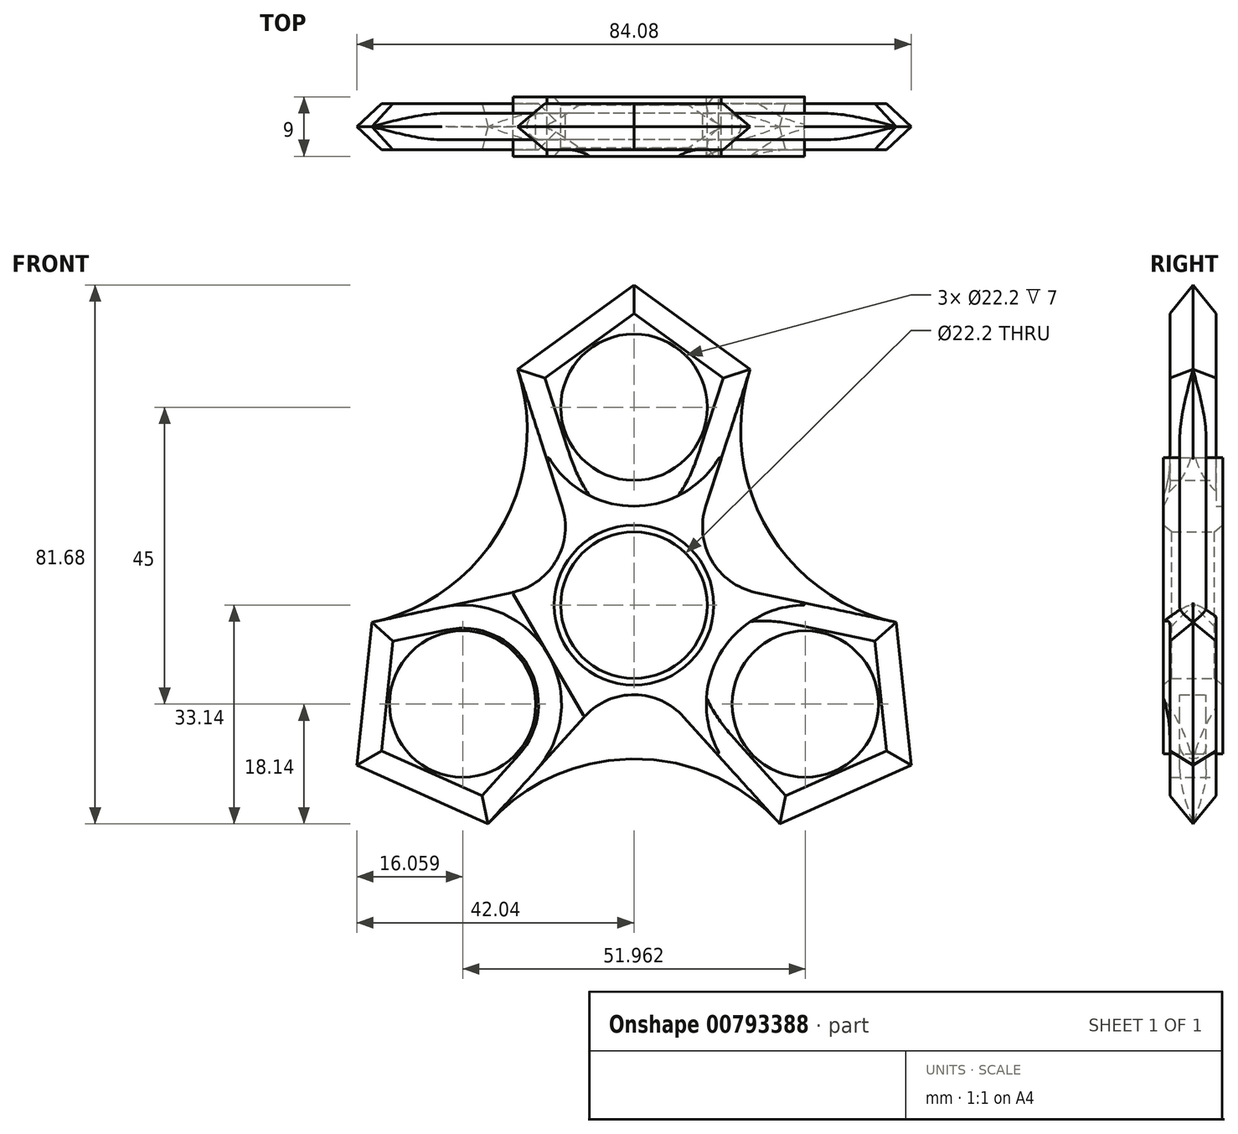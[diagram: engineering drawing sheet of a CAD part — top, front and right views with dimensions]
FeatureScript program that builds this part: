
annotation { "Feature Type Name" : "Feature", "Feature Type Description" : "" }
export const myFeature = defineFeature(function(context is Context, id is Id, definition is map)
    precondition{}
    {
        {
            var Q0;
            Q0=qCreatedBy(makeId("Front.planeOp"),FACE);
            var sketch = newSketch(context, id + "F0", { "sketchPlane" : qUnion([Q0])});
            skCircle(sketch, "E0", {"center": v(0, 0) * mm, "radius": 4 * mm});
            skCircle(sketch, "E1", {"center": v(0, 0) * mm, "radius": 11.1 * mm});
            skCircle(sketch, "E2", {"center": v(0, 30) * mm, "radius": 4 * mm});
            skCircle(sketch, "E3", {"center": v(0, 30) * mm, "radius": 11.1 * mm});
            skCircle(sketch, "E4.1.0", {"center": v(-25.98, -15) * mm, "radius": 11.1 * mm});
            skCircle(sketch, "E4.1.1", {"center": v(-25.98, -15) * mm, "radius": 4 * mm});
            skCircle(sketch, "E4.2.0", {"center": v(25.98, -15) * mm, "radius": 11.1 * mm});
            skCircle(sketch, "E4.2.1", {"center": v(25.98, -15) * mm, "radius": 4 * mm});
            skCircle(sketch, "E5.cCircle", {"center": v(0, 30) * mm, "radius": 15 * mm, "construction": true});
            skLineSegment(sketch, "E5.0", {"start": v(10.9, 15) * mm, "end": v(-10.9, 15) * mm});
            skLineSegment(sketch, "E5.1", {"start": v(-10.9, 15) * mm, "end": v(-17.63, 35.73) * mm});
            skLineSegment(sketch, "E5.2", {"start": v(-17.63, 35.73) * mm, "end": v(0, 48.54) * mm});
            skLineSegment(sketch, "E5.3", {"start": v(0, 48.54) * mm, "end": v(17.63, 35.73) * mm});
            skLineSegment(sketch, "E5.4", {"start": v(17.63, 35.73) * mm, "end": v(10.9, 15) * mm});
            skPoint(sketch, "E5.0.midPoint", {"position": v(0, 15) * mm});
            skLineSegment(sketch, "E6.1.0", {"start": v(-39.76, -2.6) * mm, "end": v(-18.44, 1.94) * mm});
            skLineSegment(sketch, "E6.1.2", {"start": v(-7.54, -16.94) * mm, "end": v(-22.13, -33.14) * mm});
            skLineSegment(sketch, "E6.1.3", {"start": v(-22.13, -33.14) * mm, "end": v(-42.04, -24.27) * mm});
            skLineSegment(sketch, "E6.1.4", {"start": v(-42.04, -24.27) * mm, "end": v(-39.76, -2.6) * mm});
            skCircle(sketch, "E6.1.5", {"center": v(-25.98, -15) * mm, "radius": 15 * mm, "construction": true});
            skLineSegment(sketch, "E6.2.0", {"start": v(22.13, -33.14) * mm, "end": v(7.54, -16.94) * mm});
            skLineSegment(sketch, "E6.2.1", {"start": v(7.54, -16.94) * mm, "end": v(18.44, 1.94) * mm});
            skLineSegment(sketch, "E6.2.2", {"start": v(18.44, 1.94) * mm, "end": v(39.76, -2.6) * mm});
            skLineSegment(sketch, "E6.2.3", {"start": v(39.76, -2.6) * mm, "end": v(42.04, -24.27) * mm});
            skLineSegment(sketch, "E6.2.4", {"start": v(42.04, -24.27) * mm, "end": v(22.13, -33.14) * mm});
            skCircle(sketch, "E6.2.5", {"center": v(25.98, -15) * mm, "radius": 15 * mm, "construction": true});
            skArc(sketch, "E7", {"start": v(-18.44, 1.94) * mm, "mid": v(-11.76, 6.8) * mm, "end": v(-10.9, 15) * mm});
            skArc(sketch, "E8", {"start": v(7.54, -16.94) * mm, "mid": v(0, -13.58) * mm, "end": v(-7.54, -16.94) * mm});
            skArc(sketch, "E9", {"start": v(-39.76, -2.6) * mm, "mid": v(-20.17, 11.64) * mm, "end": v(-17.63, 35.73) * mm});
            skArc(sketch, "E10", {"start": v(22.13, -33.14) * mm, "mid": v(0, -23.28) * mm, "end": v(-22.13, -33.14) * mm});
            skArc(sketch, "E11", {"start": v(17.63, 35.73) * mm, "mid": v(20.17, 11.64) * mm, "end": v(39.76, -2.6) * mm});
            skArc(sketch, "E12", {"start": v(10.9, 15) * mm, "mid": v(11.76, 6.8) * mm, "end": v(18.44, 1.94) * mm});
            skArc(sketch, "E13", {"start": v(-10.9, 15) * mm, "mid": v(-9.52, 11.37) * mm, "end": v(-7.8, 7.89) * mm});
            skArc(sketch, "E14", {"start": v(18.44, 1.94) * mm, "mid": v(14.6, 2.56) * mm, "end": v(10.74, 2.82) * mm});
            skArc(sketch, "E15", {"start": v(-7.54, -16.94) * mm, "mid": v(-5.09, -13.93) * mm, "end": v(-2.93, -10.7) * mm});
            skArc(sketch, "E16", {"start": v(10.9, 15) * mm, "mid": v(9.52, 11.37) * mm, "end": v(7.8, 7.89) * mm});
            skArc(sketch, "E17", {"start": v(7.54, -16.94) * mm, "mid": v(5.09, -13.93) * mm, "end": v(2.93, -10.7) * mm});
            skArc(sketch, "E18", {"start": v(-18.44, 1.94) * mm, "mid": v(-14.6, 2.56) * mm, "end": v(-10.74, 2.82) * mm});
            skArc(sketch, "E19", {"start": v(-29.1, -0.33) * mm, "mid": v(-13, -7.5) * mm, "end": v(-14.83, -25.04) * mm});
            skArc(sketch, "E20", {"start": v(-14.27, 25.36) * mm, "mid": v(0, 15) * mm, "end": v(14.27, 25.36) * mm});
            skArc(sketch, "E21", {"start": v(29.1, -0.33) * mm, "mid": v(13, -7.5) * mm, "end": v(14.83, -25.04) * mm});
            skLineSegment(sketch, "E22", {"start": v(-18.44, 1.94) * mm, "end": v(-7.54, -16.94) * mm});
            skPoint(sketch, "E23", {"position": v(-13, -7.5) * mm});
            skPoint(sketch, "E24", {"position": v(13, -7.5) * mm});
            skSolve(sketch);
        }
        {
            var Q0;
            Q0=makeQuery(id+"F0.imprint","IMPRINT",FACE,{"disambiguationData":[TD([[makeQuery(id+"F0.imprint","IMPRINT",EDGE,{"derivedFrom":sQuery(id+"F0.wireOp",EDGE,"E6.1.1")}),1.0]])]});
            var Q1;
            Q1=makeQuery(id+"F0.imprint","IMPRINT",FACE,{"disambiguationData":[TD([[makeQuery(id+"F0.imprint","IMPRINT",EDGE,{"derivedFrom":sQuery(id+"F0.wireOp",EDGE,"E3")}),-1.0]])]});
            var Q2;
            Q2=makeQuery(id+"F0.imprint","IMPRINT",FACE,{"disambiguationData":[TD([[makeQuery(id+"F0.imprint","IMPRINT",EDGE,{"derivedFrom":sQuery(id+"F0.wireOp",EDGE,"E4.1.0")}),-1.0]])]});
            var Q3;
            Q3=makeQuery(id+"F0.imprint","IMPRINT",FACE,{"disambiguationData":[TD([[makeQuery(id+"F0.imprint","IMPRINT",EDGE,{"derivedFrom":sQuery(id+"F0.wireOp",EDGE,"E4.2.0")}),-1.0]])]});
            extrude(context, id + "F1", {"entities" : qUnion([Q0, Q1, Q2, Q3]), "endBound" : BoundingType.SYMMETRIC, "depth" : 7 * mm, "offsetDistance" : 25 * mm});
        }
        {
            var Q0;
            {var subQ3=sQuery(id+"F0.wireOp",EDGE,"1cefd3b2-24fc-483e-bb30-bab2c45d141c.0");Q0=makeQuery(id+"F0.imprint","IMPRINT",FACE,{"disambiguationData":[TD([[makeQuery(id+"F0.imprint","IMPRINT",EDGE,{"derivedFrom":subQ3}),-1.0]])]});}
            var Q1;
            {var subQ0=sQuery(id+"F0.wireOp",EDGE,"E6.2.2");var subQ3=sQuery(id+"F0.wireOp",EDGE,"E21");var subQ5=makeQuery(id+"F0.imprint","INTERSECT",VERTEX,{"derivedFrom":[subQ0,subQ3]});Q1=makeQuery(id+"F0.imprint","IMPRINT",FACE,{"disambiguationData":[TD([[makeQuery(id+"F0.imprint","IMPRINT",EDGE,{"disambiguationData":[TD([[subQ5,-1.0]])],"derivedFrom":subQ3}),-1.0]])]});}
            var Q2;
            {var subQ1=sQuery(id+"F0.wireOp",EDGE,"E6.2.0");var subQ3=sQuery(id+"F0.wireOp",EDGE,"E21");var subQ4=makeQuery(id+"F0.imprint","INTERSECT",VERTEX,{"derivedFrom":[subQ1,subQ3]});Q2=makeQuery(id+"F0.imprint","IMPRINT",FACE,{"disambiguationData":[TD([[makeQuery(id+"F0.imprint","IMPRINT",EDGE,{"disambiguationData":[TD([[subQ4,1.0]])],"derivedFrom":subQ3}),-1.0]])]});}
            var Q3;
            {var subQ3=sQuery(id+"F0.wireOp",EDGE,"3a486683-1fc8-4559-9607-c20eb6ca9e57.trimOffspring");Q3=makeQuery(id+"F0.imprint","IMPRINT",FACE,{"disambiguationData":[TD([[makeQuery(id+"F0.imprint","IMPRINT",EDGE,{"derivedFrom":subQ3}),-1.0]])]});}
            var Q4;
            {var subQ0=sQuery(id+"F0.wireOp",EDGE,"E5.4");var subQ3=sQuery(id+"F0.wireOp",EDGE,"E20");var subQ5=makeQuery(id+"F0.imprint","INTERSECT",VERTEX,{"derivedFrom":[subQ0,subQ3]});Q4=makeQuery(id+"F0.imprint","IMPRINT",FACE,{"disambiguationData":[TD([[makeQuery(id+"F0.imprint","IMPRINT",EDGE,{"disambiguationData":[TD([[subQ5,1.0]])],"derivedFrom":subQ3}),-1.0]])]});}
            var Q5;
            {var subQ4=sQuery(id+"F0.wireOp",EDGE,"E7");Q5=makeQuery(id+"F0.imprint","IMPRINT",FACE,{"disambiguationData":[TD([[makeQuery(id+"F0.imprint","IMPRINT",EDGE,{"derivedFrom":subQ4}),-1.0]])]});}
            var Q6;
            {var subQ4=sQuery(id+"F0.wireOp",EDGE,"E12");Q6=makeQuery(id+"F0.imprint","IMPRINT",FACE,{"disambiguationData":[TD([[makeQuery(id+"F0.imprint","IMPRINT",EDGE,{"derivedFrom":subQ4}),-1.0]])]});}
            var Q7;
            {var subQ4=sQuery(id+"F0.wireOp",EDGE,"E8");Q7=makeQuery(id+"F0.imprint","IMPRINT",FACE,{"disambiguationData":[TD([[makeQuery(id+"F0.imprint","IMPRINT",EDGE,{"derivedFrom":subQ4}),-1.0]])]});}
            var Q8;
            {var subQ5=sQuery(id+"F0.wireOp",EDGE,"1cefd3b2-24fc-483e-bb30-bab2c45d141c.0");Q8=makeQuery(id+"F0.imprint","IMPRINT",FACE,{"disambiguationData":[TD([[makeQuery(id+"F0.imprint","IMPRINT",EDGE,{"derivedFrom":subQ5}),1.0]])]});}
            var Q9;
            {var subQ5=sQuery(id+"F0.wireOp",EDGE,"c63e2d2c-fdf0-4c3a-aaa4-641683c2e66b.trimOffspring");Q9=makeQuery(id+"F0.imprint","IMPRINT",FACE,{"disambiguationData":[TD([[makeQuery(id+"F0.imprint","IMPRINT",EDGE,{"derivedFrom":subQ5}),1.0]])]});}
            var Q10;
            {var subQ5=sQuery(id+"F0.wireOp",EDGE,"3a486683-1fc8-4559-9607-c20eb6ca9e57.trimOffspring");Q10=makeQuery(id+"F0.imprint","IMPRINT",FACE,{"disambiguationData":[TD([[makeQuery(id+"F0.imprint","IMPRINT",EDGE,{"derivedFrom":subQ5}),1.0]])]});}
            var Q11;
            {var subQ1=sQuery(id+"F0.wireOp",EDGE,"E6.1.0");var subQ3=sQuery(id+"F0.wireOp",EDGE,"E19");var subQ4=makeQuery(id+"F0.imprint","INTERSECT",VERTEX,{"derivedFrom":[subQ1,subQ3]});Q11=makeQuery(id+"F0.imprint","IMPRINT",FACE,{"disambiguationData":[TD([[makeQuery(id+"F0.imprint","IMPRINT",EDGE,{"disambiguationData":[TD([[subQ4,-1.0]])],"derivedFrom":subQ3}),1.0]])]});}
            var Q12;
            {var subQ1=sQuery(id+"F0.wireOp",EDGE,"E6.1.2");var subQ3=sQuery(id+"F0.wireOp",EDGE,"E19");var subQ4=makeQuery(id+"F0.imprint","INTERSECT",VERTEX,{"derivedFrom":[subQ1,subQ3]});Q12=makeQuery(id+"F0.imprint","IMPRINT",FACE,{"disambiguationData":[TD([[makeQuery(id+"F0.imprint","IMPRINT",EDGE,{"disambiguationData":[TD([[subQ4,1.0]])],"derivedFrom":subQ3}),1.0]])]});}
            var Q13;
            {var subQ3=sQuery(id+"F0.wireOp",EDGE,"c63e2d2c-fdf0-4c3a-aaa4-641683c2e66b.trimOffspring");Q13=makeQuery(id+"F0.imprint","IMPRINT",FACE,{"disambiguationData":[TD([[makeQuery(id+"F0.imprint","IMPRINT",EDGE,{"derivedFrom":subQ3}),-1.0]])]});}
            var Q14;
            {var subQ0=sQuery(id+"F0.wireOp",EDGE,"E5.1");var subQ3=sQuery(id+"F0.wireOp",EDGE,"E20");var subQ5=makeQuery(id+"F0.imprint","INTERSECT",VERTEX,{"derivedFrom":[subQ0,subQ3]});Q14=makeQuery(id+"F0.imprint","IMPRINT",FACE,{"disambiguationData":[TD([[makeQuery(id+"F0.imprint","IMPRINT",EDGE,{"disambiguationData":[TD([[subQ5,-1.0]])],"derivedFrom":subQ3}),-1.0]])]});}
            var Q15;
            {var subQ0=sQuery(id+"F0.wireOp",EDGE,"E13");Q15=makeQuery(id+"F0.imprint","IMPRINT",FACE,{"disambiguationData":[TD([[makeQuery(id+"F0.imprint","IMPRINT",EDGE,{"derivedFrom":subQ0}),1.0]])]});}
            var Q16;
            {var subQ0=sQuery(id+"F0.wireOp",EDGE,"E14");Q16=makeQuery(id+"F0.imprint","IMPRINT",FACE,{"disambiguationData":[TD([[makeQuery(id+"F0.imprint","IMPRINT",EDGE,{"derivedFrom":subQ0}),1.0]])]});}
            var Q17;
            {var subQ3=sQuery(id+"F0.wireOp",EDGE,"E15");Q17=makeQuery(id+"F0.imprint","IMPRINT",FACE,{"disambiguationData":[TD([[makeQuery(id+"F0.imprint","IMPRINT",EDGE,{"derivedFrom":subQ3}),1.0]])]});}
            extrude(context, id + "F2", {"entities" : qUnion([Q0, Q1, Q2, Q3, Q4, Q5, Q6, Q7, Q8, Q9, Q10, Q11, Q12, Q13, Q14, Q15, Q16, Q17]), "operationType" : NewBodyOperationType.ADD, "endBound" : BoundingType.SYMMETRIC, "depth" : 9 * mm, "offsetDistance" : 25 * mm});
        }
        {
            var Q0;
            Q0=makeQuery(id+"F1.opExtrude","CAP_EDGE",EDGE,{"disambiguationData":[OSD([sQuery(id+"F0.wireOp",EDGE,"E6.1.3")])],"isStart":false});
            var Q1;
            Q1=makeQuery(id+"F1.opExtrude","CAP_EDGE",EDGE,{"disambiguationData":[OSD([sQuery(id+"F0.wireOp",EDGE,"E6.1.4")])],"isStart":false});
            var Q2;
            Q2=makeQuery(id+"F1.opExtrude","CAP_EDGE",EDGE,{"disambiguationData":[OSD([sQuery(id+"F0.wireOp",EDGE,"E6.1.3")])],"isStart":true});
            var Q3;
            Q3=makeQuery(id+"F1.opExtrude","CAP_EDGE",EDGE,{"disambiguationData":[OSD([sQuery(id+"F0.wireOp",EDGE,"E5.2")])],"isStart":false});
            var Q4;
            Q4=makeQuery(id+"F1.opExtrude","CAP_EDGE",EDGE,{"disambiguationData":[OSD([sQuery(id+"F0.wireOp",EDGE,"E5.3")])],"isStart":false});
            var Q5;
            Q5=makeQuery(id+"F1.opExtrude","CAP_EDGE",EDGE,{"disambiguationData":[OSD([sQuery(id+"F0.wireOp",EDGE,"E5.2")])],"isStart":true});
            var Q6;
            Q6=makeQuery(id+"F1.opExtrude","CAP_EDGE",EDGE,{"disambiguationData":[OSD([sQuery(id+"F0.wireOp",EDGE,"E6.2.3")])],"isStart":true});
            var Q7;
            Q7=makeQuery(id+"F1.opExtrude","CAP_EDGE",EDGE,{"disambiguationData":[OSD([sQuery(id+"F0.wireOp",EDGE,"E6.2.4")])],"isStart":true});
            var Q8;
            Q8=makeQuery(id+"F1.opExtrude","CAP_EDGE",EDGE,{"disambiguationData":[OSD([sQuery(id+"F0.wireOp",EDGE,"E6.2.3")])],"isStart":false});
            var Q9;
            Q9=makeQuery(id+"F1.opExtrude","CAP_EDGE",EDGE,{"disambiguationData":[OSD([sQuery(id+"F0.wireOp",EDGE,"E6.2.4")])],"isStart":false});
            var Q10;
            Q10=makeQuery(id+"F1.opExtrude","CAP_EDGE",EDGE,{"disambiguationData":[OSD([sQuery(id+"F0.wireOp",EDGE,"E5.3")])],"isStart":true});
            var Q11;
            Q11=makeQuery(id+"F1.opExtrude","CAP_EDGE",EDGE,{"disambiguationData":[OSD([sQuery(id+"F0.wireOp",EDGE,"E6.1.4")])],"isStart":true});
            var Q12;
            Q12=makeQuery(id+"F1.opExtrude","CAP_EDGE",EDGE,{"disambiguationData":[OSD([sQuery(id+"F0.wireOp",EDGE,"E6.2.2")])],"isStart":false});
            var Q13;
            Q13=makeQuery(id+"F1.opExtrude","CAP_EDGE",EDGE,{"disambiguationData":[OSD([sQuery(id+"F0.wireOp",EDGE,"E6.2.2")])],"isStart":true});
            var Q14;
            Q14=makeQuery(id+"F1.opExtrude","CAP_EDGE",EDGE,{"disambiguationData":[OSD([sQuery(id+"F0.wireOp",EDGE,"E5.4")])],"isStart":true});
            var Q15;
            Q15=makeQuery(id+"F1.opExtrude","CAP_EDGE",EDGE,{"disambiguationData":[OSD([sQuery(id+"F0.wireOp",EDGE,"E5.4")])],"isStart":false});
            var Q16;
            Q16=makeQuery(id+"F1.opExtrude","CAP_EDGE",EDGE,{"disambiguationData":[OSD([sQuery(id+"F0.wireOp",EDGE,"E6.2.0")])],"isStart":false});
            var Q17;
            Q17=makeQuery(id+"F1.opExtrude","CAP_EDGE",EDGE,{"disambiguationData":[OSD([sQuery(id+"F0.wireOp",EDGE,"E6.2.0")])],"isStart":true});
            var Q18;
            Q18=makeQuery(id+"F1.opExtrude","CAP_EDGE",EDGE,{"disambiguationData":[OSD([sQuery(id+"F0.wireOp",EDGE,"E5.1")])],"isStart":true});
            var Q19;
            Q19=makeQuery(id+"F1.opExtrude","CAP_EDGE",EDGE,{"disambiguationData":[OSD([sQuery(id+"F0.wireOp",EDGE,"E5.1")])],"isStart":false});
            var Q20;
            Q20=makeQuery(id+"F1.opExtrude","CAP_EDGE",EDGE,{"disambiguationData":[OSD([sQuery(id+"F0.wireOp",EDGE,"E6.1.0")])],"isStart":true});
            var Q21;
            Q21=makeQuery(id+"F1.opExtrude","CAP_EDGE",EDGE,{"disambiguationData":[OSD([sQuery(id+"F0.wireOp",EDGE,"E6.1.0")])],"isStart":false});
            var Q22;
            Q22=makeQuery(id+"F1.opExtrude","CAP_EDGE",EDGE,{"disambiguationData":[OSD([sQuery(id+"F0.wireOp",EDGE,"E6.1.2")])],"isStart":true});
            var Q23;
            Q23=makeQuery(id+"F1.opExtrude","CAP_EDGE",EDGE,{"disambiguationData":[OSD([sQuery(id+"F0.wireOp",EDGE,"E6.1.2")])],"isStart":false});
            chamfer(context, id + "F3", {"entities" : qUnion([Q0, Q1, Q2, Q3, Q4, Q5, Q6, Q7, Q8, Q9, Q10, Q11, Q12, Q13, Q14, Q15, Q16, Q17, Q18, Q19, Q20, Q21, Q22, Q23]), "chamferType" : ChamferType.OFFSET_ANGLE, "width" : 3.5 * mm, "oppositeDirection" : false, "angle" : 45 * degree, "tangentPropagation" : true});
        }
        {
            var Q0;
            {var subQ0=sQuery(id+"F0.wireOp",EDGE,"E6.1.2");var subQ1=sQuery(id+"F0.wireOp",EDGE,"E19");var subQ2=sQuery(id+"F0.wireOp",EDGE,"E6.1.0");Q0=makeQuery(id+"F2.boolean.opBoolean","SPLIT",EDGE,{"disambiguationData":[TD([makeQuery(id+"F1.opExtrude","CAP_FACE",FACE,{"disambiguationData":[OSD([sQuery(id+"F0.wireOp",EDGE,"E4.1.0"),subQ2,subQ0,sQuery(id+"F0.wireOp",EDGE,"E6.1.3"),sQuery(id+"F0.wireOp",EDGE,"E6.1.4"),subQ1])],"isStart":false})])],"derivedFrom":makeQuery(id+"F2.opExtrude","SWEPT_EDGE",EDGE,{"disambiguationData":[OSD([subQ0,subQ1])]})});}
            var Q1;
            {var subQ0=sQuery(id+"F0.wireOp",EDGE,"E6.2.0");var subQ1=sQuery(id+"F0.wireOp",EDGE,"E21");var subQ2=sQuery(id+"F0.wireOp",EDGE,"E6.2.2");Q1=makeQuery(id+"F2.boolean.opBoolean","SPLIT",EDGE,{"disambiguationData":[TD([makeQuery(id+"F1.opExtrude","CAP_FACE",FACE,{"disambiguationData":[OSD([sQuery(id+"F0.wireOp",EDGE,"E4.2.0"),subQ0,subQ2,sQuery(id+"F0.wireOp",EDGE,"E6.2.3"),sQuery(id+"F0.wireOp",EDGE,"E6.2.4"),subQ1])],"isStart":false})])],"derivedFrom":makeQuery(id+"F2.opExtrude","SWEPT_EDGE",EDGE,{"disambiguationData":[OSD([subQ0,subQ1])]})});}
            var Q2;
            {var subQ0=sQuery(id+"F0.wireOp",EDGE,"E6.2.2");var subQ1=sQuery(id+"F0.wireOp",EDGE,"E21");var subQ2=sQuery(id+"F0.wireOp",EDGE,"E6.2.0");Q2=makeQuery(id+"F2.boolean.opBoolean","SPLIT",EDGE,{"disambiguationData":[TD([makeQuery(id+"F1.opExtrude","CAP_FACE",FACE,{"disambiguationData":[OSD([sQuery(id+"F0.wireOp",EDGE,"E4.2.0"),subQ2,subQ0,sQuery(id+"F0.wireOp",EDGE,"E6.2.3"),sQuery(id+"F0.wireOp",EDGE,"E6.2.4"),subQ1])],"isStart":false})])],"derivedFrom":makeQuery(id+"F2.opExtrude","SWEPT_EDGE",EDGE,{"disambiguationData":[OSD([subQ0,subQ1])]})});}
            var Q3;
            {var subQ0=sQuery(id+"F0.wireOp",EDGE,"E6.2.2");var subQ1=sQuery(id+"F0.wireOp",EDGE,"E21");var subQ2=sQuery(id+"F0.wireOp",EDGE,"E6.2.0");Q3=makeQuery(id+"F2.boolean.opBoolean","SPLIT",EDGE,{"disambiguationData":[TD([makeQuery(id+"F1.opExtrude","CAP_FACE",FACE,{"disambiguationData":[OSD([sQuery(id+"F0.wireOp",EDGE,"E4.2.0"),subQ2,subQ0,sQuery(id+"F0.wireOp",EDGE,"E6.2.3"),sQuery(id+"F0.wireOp",EDGE,"E6.2.4"),subQ1])],"isStart":true})])],"derivedFrom":makeQuery(id+"F2.opExtrude","SWEPT_EDGE",EDGE,{"disambiguationData":[OSD([subQ0,subQ1])]})});}
            var Q4;
            {var subQ0=sQuery(id+"F0.wireOp",EDGE,"E20");var subQ1=sQuery(id+"F0.wireOp",EDGE,"E5.4");var subQ2=sQuery(id+"F0.wireOp",EDGE,"E5.1");Q4=makeQuery(id+"F2.boolean.opBoolean","SPLIT",EDGE,{"disambiguationData":[TD([makeQuery(id+"F1.opExtrude","CAP_FACE",FACE,{"disambiguationData":[OSD([sQuery(id+"F0.wireOp",EDGE,"E3"),subQ2,sQuery(id+"F0.wireOp",EDGE,"E5.2"),sQuery(id+"F0.wireOp",EDGE,"E5.3"),subQ1,subQ0])],"isStart":true})])],"derivedFrom":makeQuery(id+"F2.opExtrude","SWEPT_EDGE",EDGE,{"disambiguationData":[OSD([subQ1,subQ0])]})});}
            var Q5;
            {var subQ0=sQuery(id+"F0.wireOp",EDGE,"E20");var subQ1=sQuery(id+"F0.wireOp",EDGE,"E5.4");var subQ2=sQuery(id+"F0.wireOp",EDGE,"E5.1");Q5=makeQuery(id+"F2.boolean.opBoolean","SPLIT",EDGE,{"disambiguationData":[TD([makeQuery(id+"F1.opExtrude","CAP_FACE",FACE,{"disambiguationData":[OSD([sQuery(id+"F0.wireOp",EDGE,"E3"),subQ2,sQuery(id+"F0.wireOp",EDGE,"E5.2"),sQuery(id+"F0.wireOp",EDGE,"E5.3"),subQ1,subQ0])],"isStart":false})])],"derivedFrom":makeQuery(id+"F2.opExtrude","SWEPT_EDGE",EDGE,{"disambiguationData":[OSD([subQ1,subQ0])]})});}
            var Q6;
            {var subQ0=sQuery(id+"F0.wireOp",EDGE,"E6.1.2");var subQ1=sQuery(id+"F0.wireOp",EDGE,"E19");var subQ2=sQuery(id+"F0.wireOp",EDGE,"E6.1.0");Q6=makeQuery(id+"F2.boolean.opBoolean","SPLIT",EDGE,{"disambiguationData":[TD([makeQuery(id+"F1.opExtrude","CAP_FACE",FACE,{"disambiguationData":[OSD([sQuery(id+"F0.wireOp",EDGE,"E4.1.0"),subQ2,subQ0,sQuery(id+"F0.wireOp",EDGE,"E6.1.3"),sQuery(id+"F0.wireOp",EDGE,"E6.1.4"),subQ1])],"isStart":true})])],"derivedFrom":makeQuery(id+"F2.opExtrude","SWEPT_EDGE",EDGE,{"disambiguationData":[OSD([subQ0,subQ1])]})});}
            var Q7;
            {var subQ0=sQuery(id+"F0.wireOp",EDGE,"E6.2.0");var subQ1=sQuery(id+"F0.wireOp",EDGE,"E21");var subQ2=sQuery(id+"F0.wireOp",EDGE,"E6.2.2");Q7=makeQuery(id+"F2.boolean.opBoolean","SPLIT",EDGE,{"disambiguationData":[TD([makeQuery(id+"F1.opExtrude","CAP_FACE",FACE,{"disambiguationData":[OSD([sQuery(id+"F0.wireOp",EDGE,"E4.2.0"),subQ0,subQ2,sQuery(id+"F0.wireOp",EDGE,"E6.2.3"),sQuery(id+"F0.wireOp",EDGE,"E6.2.4"),subQ1])],"isStart":true})])],"derivedFrom":makeQuery(id+"F2.opExtrude","SWEPT_EDGE",EDGE,{"disambiguationData":[OSD([subQ0,subQ1])]})});}
            var Q8;
            {var subQ0=sQuery(id+"F0.wireOp",EDGE,"E6.1.0");var subQ1=sQuery(id+"F0.wireOp",EDGE,"E19");var subQ2=sQuery(id+"F0.wireOp",EDGE,"E6.1.2");Q8=makeQuery(id+"F2.boolean.opBoolean","SPLIT",EDGE,{"disambiguationData":[TD([makeQuery(id+"F1.opExtrude","CAP_FACE",FACE,{"disambiguationData":[OSD([sQuery(id+"F0.wireOp",EDGE,"E4.1.0"),subQ0,subQ2,sQuery(id+"F0.wireOp",EDGE,"E6.1.3"),sQuery(id+"F0.wireOp",EDGE,"E6.1.4"),subQ1])],"isStart":false})])],"derivedFrom":makeQuery(id+"F2.opExtrude","SWEPT_EDGE",EDGE,{"disambiguationData":[OSD([subQ0,subQ1])]})});}
            var Q9;
            {var subQ0=sQuery(id+"F0.wireOp",EDGE,"E6.1.0");var subQ1=sQuery(id+"F0.wireOp",EDGE,"E19");var subQ2=sQuery(id+"F0.wireOp",EDGE,"E6.1.2");Q9=makeQuery(id+"F2.boolean.opBoolean","SPLIT",EDGE,{"disambiguationData":[TD([makeQuery(id+"F1.opExtrude","CAP_FACE",FACE,{"disambiguationData":[OSD([sQuery(id+"F0.wireOp",EDGE,"E4.1.0"),subQ0,subQ2,sQuery(id+"F0.wireOp",EDGE,"E6.1.3"),sQuery(id+"F0.wireOp",EDGE,"E6.1.4"),subQ1])],"isStart":true})])],"derivedFrom":makeQuery(id+"F2.opExtrude","SWEPT_EDGE",EDGE,{"disambiguationData":[OSD([subQ0,subQ1])]})});}
            var Q10;
            {var subQ0=sQuery(id+"F0.wireOp",EDGE,"E20");var subQ1=sQuery(id+"F0.wireOp",EDGE,"E5.4");var subQ2=sQuery(id+"F0.wireOp",EDGE,"E5.1");Q10=makeQuery(id+"F2.boolean.opBoolean","SPLIT",EDGE,{"disambiguationData":[TD([makeQuery(id+"F1.opExtrude","CAP_FACE",FACE,{"disambiguationData":[OSD([sQuery(id+"F0.wireOp",EDGE,"E3"),subQ2,sQuery(id+"F0.wireOp",EDGE,"E5.2"),sQuery(id+"F0.wireOp",EDGE,"E5.3"),subQ1,subQ0])],"isStart":true})])],"derivedFrom":makeQuery(id+"F2.opExtrude","SWEPT_EDGE",EDGE,{"disambiguationData":[OSD([subQ2,subQ0])]})});}
            var Q11;
            {var subQ0=sQuery(id+"F0.wireOp",EDGE,"E5.1");var subQ1=sQuery(id+"F0.wireOp",EDGE,"E20");var subQ2=sQuery(id+"F0.wireOp",EDGE,"E5.4");Q11=makeQuery(id+"F2.boolean.opBoolean","SPLIT",EDGE,{"disambiguationData":[TD([makeQuery(id+"F1.opExtrude","CAP_FACE",FACE,{"disambiguationData":[OSD([sQuery(id+"F0.wireOp",EDGE,"E3"),subQ0,sQuery(id+"F0.wireOp",EDGE,"E5.2"),sQuery(id+"F0.wireOp",EDGE,"E5.3"),subQ2,subQ1])],"isStart":false})])],"derivedFrom":makeQuery(id+"F2.opExtrude","SWEPT_EDGE",EDGE,{"disambiguationData":[OSD([subQ0,subQ1])]})});}
            fillet(context, id + "F4", {"entities" : qUnion([Q0, Q1, Q2, Q3, Q4, Q5, Q6, Q7, Q8, Q9, Q10, Q11]), "radius" : .2 * mm, "tangentPropagation" : true, "allowEdgeOverflow" : false});
        }
        {
            var Q0;
            Q0=makeQuery(id+"F1.opExtrude","CAP_EDGE",EDGE,{"disambiguationData":[OSD([sQuery(id+"F0.wireOp",EDGE,"E21")])],"isStart":false});
            var Q1;
            Q1=makeQuery(id+"F1.opExtrude","CAP_EDGE",EDGE,{"disambiguationData":[OSD([sQuery(id+"F0.wireOp",EDGE,"E21")])],"isStart":true});
            var Q2;
            Q2=makeQuery(id+"F1.opExtrude","CAP_EDGE",EDGE,{"disambiguationData":[OSD([sQuery(id+"F0.wireOp",EDGE,"E20")])],"isStart":true});
            var Q3;
            Q3=makeQuery(id+"F1.opExtrude","CAP_EDGE",EDGE,{"disambiguationData":[OSD([sQuery(id+"F0.wireOp",EDGE,"E19")])],"isStart":true});
            var Q4;
            Q4=makeQuery(id+"F1.opExtrude","CAP_EDGE",EDGE,{"disambiguationData":[OSD([sQuery(id+"F0.wireOp",EDGE,"E19")])],"isStart":false});
            var Q5;
            Q5=makeQuery(id+"F1.opExtrude","CAP_EDGE",EDGE,{"disambiguationData":[OSD([sQuery(id+"F0.wireOp",EDGE,"E20")])],"isStart":false});
            fillet(context, id + "F5", {"entities" : qUnion([Q0, Q1, Q2, Q3, Q4, Q5]), "radius" : 5.5 * mm, "tangentPropagation" : true, "allowEdgeOverflow" : false});
        }
        {
            var Q0;
            Q0=makeQuery(id+"F2.opExtrude","CAP_EDGE",EDGE,{"disambiguationData":[OSD([sQuery(id+"F0.wireOp",EDGE,"E1")])],"isStart":false});
            var Q1;
            Q1=makeQuery(id+"F2.opExtrude","CAP_EDGE",EDGE,{"disambiguationData":[OSD([sQuery(id+"F0.wireOp",EDGE,"E1")])],"isStart":true});
            chamfer(context, id + "F6", {"entities" : qUnion([Q0, Q1]), "chamferType" : ChamferType.TWO_OFFSETS, "width1" : 1.25 * mm, "oppositeDirection" : false, "width2" : 1 * mm, "tangentPropagation" : true});
        }
        {
            var Q0;
            {var subQ0=sQuery(id+"F0.wireOp",EDGE,"E7");Q0=makeQuery(id+"F0.imprint","IMPRINT",FACE,{"disambiguationData":[TD([[makeQuery(id+"F0.imprint","IMPRINT",EDGE,{"derivedFrom":subQ0}),1.0]])]});}
            var Q1;
            {var subQ0=sQuery(id+"F0.wireOp",EDGE,"E11");Q1=makeQuery(id+"F0.imprint","IMPRINT",FACE,{"disambiguationData":[TD([[makeQuery(id+"F0.imprint","IMPRINT",EDGE,{"derivedFrom":subQ0}),-1.0]])]});}
            var Q2;
            {var subQ5=sQuery(id+"F0.wireOp",EDGE,"E8");Q2=makeQuery(id+"F0.imprint","IMPRINT",FACE,{"disambiguationData":[TD([[makeQuery(id+"F0.imprint","IMPRINT",EDGE,{"derivedFrom":subQ5}),1.0]])]});}
            extrude(context, id + "F7", {"entities" : qUnion([Q0, Q1, Q2]), "endBound" : BoundingType.SYMMETRIC, "depth" : 4 * mm, "offsetDistance" : 25 * mm});
        }
        {
            var Q0;
            Q0=makeQuery(id+"F7.opExtrude","CAP_EDGE",EDGE,{"disambiguationData":[OSD([sQuery(id+"F0.wireOp",EDGE,"E9")])],"isStart":false});
            var Q1;
            Q1=makeQuery(id+"F7.opExtrude","CAP_EDGE",EDGE,{"disambiguationData":[OSD([sQuery(id+"F0.wireOp",EDGE,"E9")])],"isStart":true});
            var Q2;
            Q2=makeQuery(id+"F7.opExtrude","CAP_EDGE",EDGE,{"disambiguationData":[OSD([sQuery(id+"F0.wireOp",EDGE,"E10")])],"isStart":false});
            var Q3;
            Q3=makeQuery(id+"F7.opExtrude","CAP_EDGE",EDGE,{"disambiguationData":[OSD([sQuery(id+"F0.wireOp",EDGE,"E10")])],"isStart":true});
            var Q4;
            Q4=makeQuery(id+"F7.opExtrude","CAP_EDGE",EDGE,{"disambiguationData":[OSD([sQuery(id+"F0.wireOp",EDGE,"E11")])],"isStart":true});
            var Q5;
            Q5=makeQuery(id+"F7.opExtrude","CAP_EDGE",EDGE,{"disambiguationData":[OSD([sQuery(id+"F0.wireOp",EDGE,"E11")])],"isStart":false});
            fillet(context, id + "F8", {"entities" : qUnion([Q0, Q1, Q2, Q3, Q4, Q5]), "radius" : 2 * mm, "tangentPropagation" : true, "allowEdgeOverflow" : false});
        }
    });
